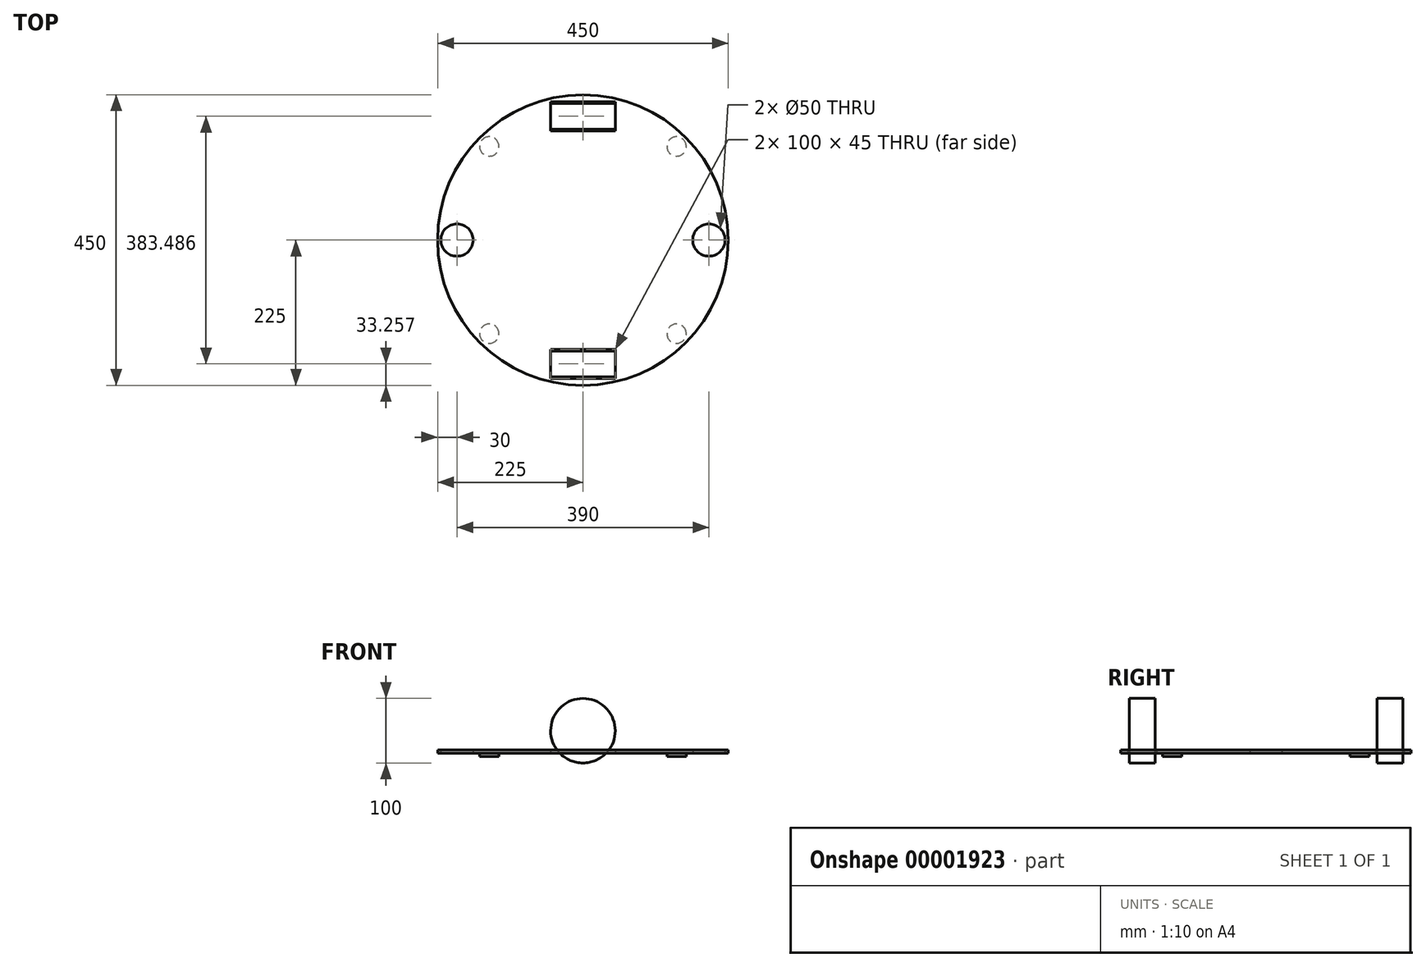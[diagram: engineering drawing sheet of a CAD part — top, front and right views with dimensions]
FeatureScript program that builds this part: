
annotation { "Feature Type Name" : "Feature", "Feature Type Description" : "" }
export const myFeature = defineFeature(function(context is Context, id is Id, definition is map)
    precondition{}
    {
        {
            var Q0;
            Q0=qCreatedBy(makeId("Top.planeOp"),FACE);
            var sketch = newSketch(context, id + "F0", { "sketchPlane" : qUnion([Q0])});
            skCircle(sketch, "E0", {"center": v(0, 0) * mm, "radius": 225 * mm});
            skLineSegment(sketch, "E1", {"start": v(-264.15, 0) * mm, "end": v(308.92, 0) * mm, "construction": true});
            skLineSegment(sketch, "E2", {"start": v(0, -253) * mm, "end": v(0, 259.46) * mm, "construction": true});
            skLineSegment(sketch, "E3", {"start": v(-238.72, -238.72) * mm, "end": v(226.13, 226.13) * mm, "construction": true});
            skLineSegment(sketch, "E4", {"start": v(229.16, -229.16) * mm, "end": v(-246.36, 246.36) * mm, "construction": true});
            skLineSegment(sketch, "E5.bottom", {"start": v(-50, 214.24) * mm, "end": v(50, 214.24) * mm});
            skLineSegment(sketch, "E5.top", {"start": v(-50, 169.24) * mm, "end": v(50, 169.24) * mm});
            skLineSegment(sketch, "E5.left", {"start": v(-50, 214.24) * mm, "end": v(-50, 169.24) * mm});
            skLineSegment(sketch, "E5.right", {"start": v(50, 214.24) * mm, "end": v(50, 169.24) * mm});
            skLineSegment(sketch, "E6.bottom", {"start": v(-50, -169.24) * mm, "end": v(50, -169.24) * mm});
            skLineSegment(sketch, "E6.top", {"start": v(-50, -214.24) * mm, "end": v(50, -214.24) * mm});
            skLineSegment(sketch, "E6.left", {"start": v(-50, -169.24) * mm, "end": v(-50, -214.24) * mm});
            skLineSegment(sketch, "E6.right", {"start": v(50, -169.24) * mm, "end": v(50, -214.24) * mm});
            skPoint(sketch, "E7", {"position": v(0, 169.24) * mm});
            skPoint(sketch, "E8", {"position": v(0, -169.24) * mm});
            skCircle(sketch, "E9", {"center": v(-144.96, 144.96) * mm, "radius": 15 * mm});
            skCircle(sketch, "E10", {"center": v(144.96, 144.96) * mm, "radius": 15 * mm});
            skCircle(sketch, "E11", {"center": v(144.96, -144.96) * mm, "radius": 15 * mm});
            skCircle(sketch, "E12", {"center": v(-144.96, -144.96) * mm, "radius": 15 * mm});
            skCircle(sketch, "E13", {"center": v(0, 0) * mm, "radius": 220 * mm, "construction": true});
            skCircle(sketch, "E14", {"center": v(-195, 0) * mm, "radius": 25 * mm});
            skCircle(sketch, "E15", {"center": v(195, 0) * mm, "radius": 25 * mm});
            skLineSegment(sketch, "E16", {"start": v(50, 211.74) * mm, "end": v(-50, 211.74) * mm, "construction": true});
            skLineSegment(sketch, "E17", {"start": v(50, -211.74) * mm, "end": v(-50, -211.74) * mm, "construction": true});
            skSolve(sketch);
        }
        {
            var Q0;
            Q0=makeQuery(id+"F0.imprint","IMPRINT",FACE,{"disambiguationData":[TD([[makeQuery(id+"F0.imprint","IMPRINT",EDGE,{"derivedFrom":sQuery(id+"F0.wireOp",EDGE,"E12")}),1.0]])]});
            var Q1;
            Q1=makeQuery(id+"F0.imprint","IMPRINT",FACE,{"disambiguationData":[TD([[makeQuery(id+"F0.imprint","IMPRINT",EDGE,{"derivedFrom":sQuery(id+"F0.wireOp",EDGE,"E9")}),1.0]])]});
            var Q2;
            Q2=makeQuery(id+"F0.imprint","IMPRINT",FACE,{"disambiguationData":[TD([[makeQuery(id+"F0.imprint","IMPRINT",EDGE,{"derivedFrom":sQuery(id+"F0.wireOp",EDGE,"E10")}),1.0]])]});
            var Q3;
            Q3=makeQuery(id+"F0.imprint","IMPRINT",FACE,{"disambiguationData":[TD([[makeQuery(id+"F0.imprint","IMPRINT",EDGE,{"derivedFrom":sQuery(id+"F0.wireOp",EDGE,"E11")}),1.0]])]});
            var Q4;
            Q4=makeQuery(id+"F0.imprint","IMPRINT",FACE,{"disambiguationData":[TD([[makeQuery(id+"F0.imprint","IMPRINT",EDGE,{"derivedFrom":sQuery(id+"F0.wireOp",EDGE,"E5.bottom")}),1.0]])]});
            extrude(context, id + "F1", {"entities" : qUnion([Q0, Q1, Q2, Q3, Q4]), "depth" : 5 * mm});
        }
        {
            var Q0;
            Q0=makeQuery(id+"F0.imprint","IMPRINT",FACE,{"disambiguationData":[TD([[makeQuery(id+"F0.imprint","IMPRINT",EDGE,{"derivedFrom":sQuery(id+"F0.wireOp",EDGE,"E9")}),1.0]])]});
            var Q1;
            Q1=makeQuery(id+"F0.imprint","IMPRINT",FACE,{"disambiguationData":[TD([[makeQuery(id+"F0.imprint","IMPRINT",EDGE,{"derivedFrom":sQuery(id+"F0.wireOp",EDGE,"E10")}),1.0]])]});
            var Q2;
            Q2=makeQuery(id+"F0.imprint","IMPRINT",FACE,{"disambiguationData":[TD([[makeQuery(id+"F0.imprint","IMPRINT",EDGE,{"derivedFrom":sQuery(id+"F0.wireOp",EDGE,"E11")}),1.0]])]});
            var Q3;
            Q3=makeQuery(id+"F0.imprint","IMPRINT",FACE,{"disambiguationData":[TD([[makeQuery(id+"F0.imprint","IMPRINT",EDGE,{"derivedFrom":sQuery(id+"F0.wireOp",EDGE,"E12")}),1.0]])]});
            var Q4;
            Q4=sQuery(id+"F0.wireOp",EDGE,"E9");
            var Q5;
            Q5=sQuery(id+"F0.wireOp",EDGE,"E12");
            var Q6;
            Q6=sQuery(id+"F0.wireOp",EDGE,"E11");
            var Q7;
            Q7=sQuery(id+"F0.wireOp",EDGE,"E10");
            extrude(context, id + "F2", {"entities" : qUnion([Q0, Q1, Q2, Q3]), "surfaceEntities" : qUnion([Q4, Q5, Q6, Q7]), "oppositeDirection" : true, "depth" : 5 * mm});
        }
        {
            var Q0;
            Q0=sQuery(id+"F0.wireOp",EDGE,"E17");
            cPlane(context, id + "F3", {"entities" : qUnion([Q0]), "cplaneType" : CPlaneType.LINE_ANGLE, "offset" : 150 * mm, "angle" : 0 * degree, "width" : 150 * mm, "height" : 150 * mm});
        }
        {
            var Q0;
            Q0=qCreatedBy(id+"F3.planeOp",FACE);
            var sketch = newSketch(context, id + "F4", { "sketchPlane" : qUnion([Q0])});
            skCircle(sketch, "E18", {"center": v(0, 35) * mm, "radius": 50 * mm});
            skLineSegment(sketch, "E19", {"start": v(0, 101.95) * mm, "end": v(0, -121.04) * mm, "construction": true});
            skSolve(sketch);
        }
        {
            var Q0;
            Q0=makeQuery(id+"F4.imprint","IMPRINT",FACE,{"disambiguationData":[TD([[makeQuery(id+"F4.imprint","IMPRINT",EDGE,{"derivedFrom":sQuery(id+"F4.wireOp",EDGE,"E18")}),1.0]])]});
            extrude(context, id + "F5", {"entities" : qUnion([Q0]), "operationType" : NewBodyOperationType.ADD, "oppositeDirection" : true, "depth" : 40 * mm});
        }
        {
            var Q0;
            Q0=sQuery(id+"F0.wireOp",EDGE,"E16");
            cPlane(context, id + "F6", {"entities" : qUnion([Q0]), "cplaneType" : CPlaneType.LINE_ANGLE, "offset" : 150 * mm, "angle" : 0 * degree, "width" : 150 * mm, "height" : 150 * mm});
        }
        {
            var Q0;
            Q0=qCreatedBy(id+"F6.planeOp",FACE);
            var sketch = newSketch(context, id + "F7", { "sketchPlane" : qUnion([Q0])});
            skCircle(sketch, "E20", {"center": v(0, 35) * mm, "radius": 50 * mm});
            skSolve(sketch);
        }
        {
            var Q0;
            Q0=makeQuery(id+"F7.imprint","IMPRINT",FACE,{"disambiguationData":[TD([[makeQuery(id+"F7.imprint","IMPRINT",EDGE,{"derivedFrom":sQuery(id+"F7.wireOp",EDGE,"E20")}),1.0]])]});
            extrude(context, id + "F8", {"entities" : qUnion([Q0]), "depth" : 40 * mm});
        }
    });
